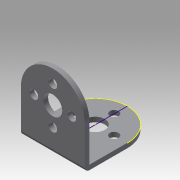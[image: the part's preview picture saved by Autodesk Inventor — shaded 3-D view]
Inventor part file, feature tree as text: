
AUTODESK INVENTOR PART (.ipt)
format: ipt  version: 2016 (Build 200138000, 138)  size: 131,584 bytes
history: native  units: in
note: dims shown in document units (in); Inventor stores cm internally (conversion verified against a paired STEP export)
features: sketch x3, other x1, imported_body x1
ambient origin geometry x8: Origin, YZ Plane, XZ Plane, XY Plane, X Axis, Y Axis, Z Axis, Center Point
bodies: Body1 (feature_tree)
feature tree (5):
  other  "BRACKET_L-ANGLE_2011"
  imported_body  "Base1"
  sketch  "Sketch1"
  sketch  "Sketch2"
  sketch  "Sketch3"
